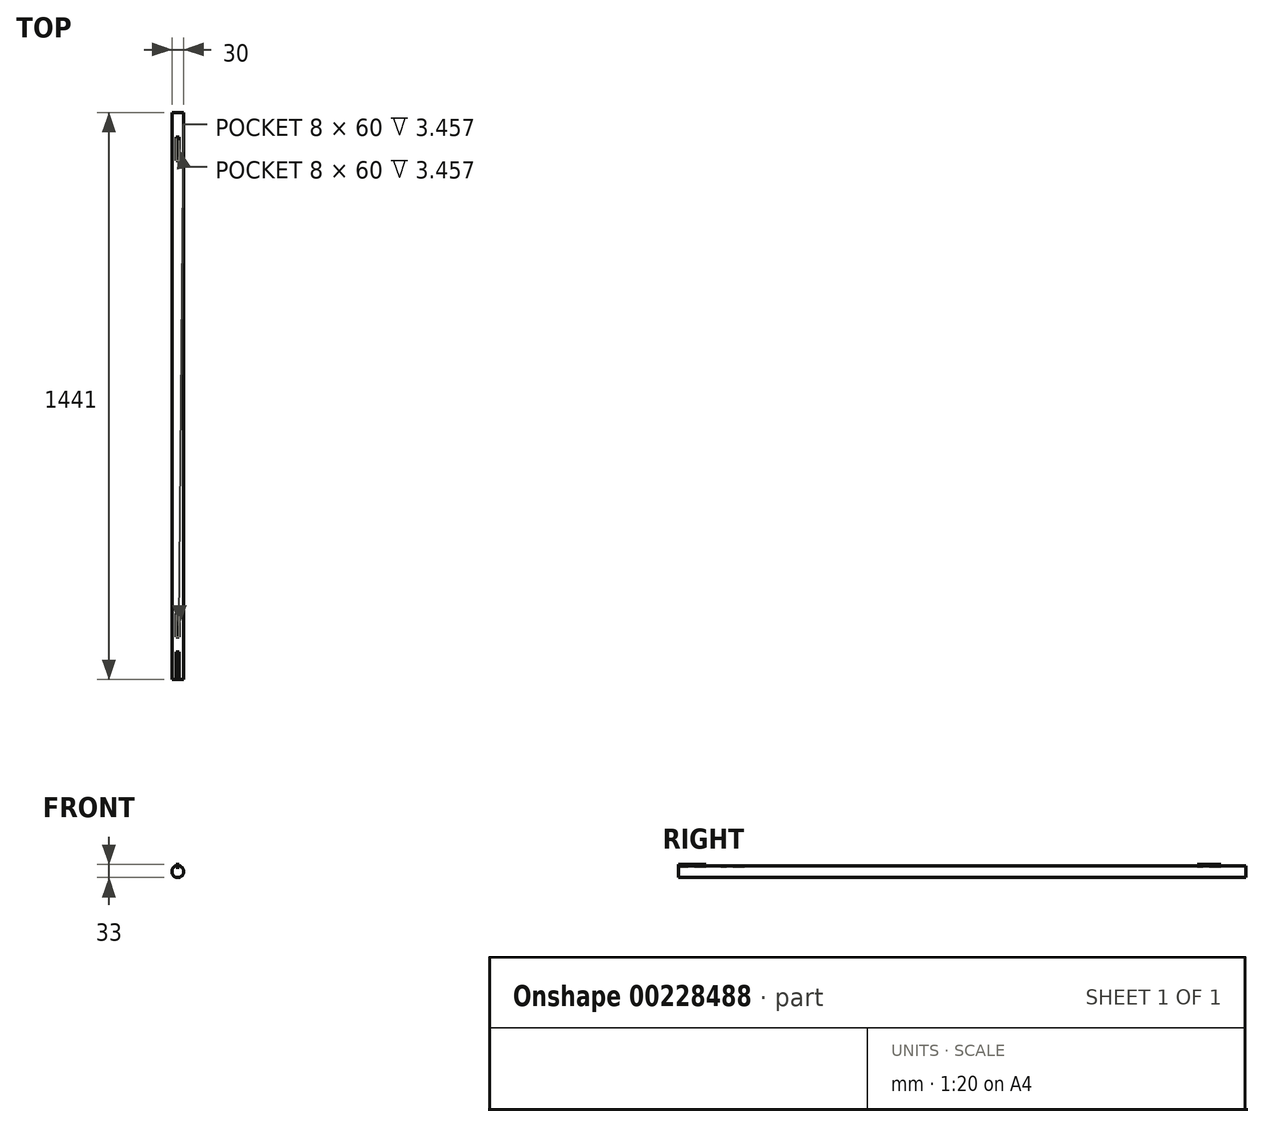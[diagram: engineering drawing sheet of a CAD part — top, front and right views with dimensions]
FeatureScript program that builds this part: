
annotation { "Feature Type Name" : "Feature", "Feature Type Description" : "" }
export const myFeature = defineFeature(function(context is Context, id is Id, definition is map)
    precondition{}
    {
        {
            var Q0;
            Q0=qCreatedBy(makeId("Front.planeOp"),FACE);
            var sketch = newSketch(context, id + "F0", { "sketchPlane" : qUnion([Q0])});
            skCircle(sketch, "E0", {"center": v(0, 0) * mm, "radius": 15 * mm});
            skSolve(sketch);
        }
        {
            var Q0;
            Q0=qSketchRegion(id+"F0",true);
            extrude(context, id + "F1", {"entities" : qUnion([Q0]), "depth" : (1441 - 698) * mm, "offsetDistance" : 25 * mm, "hasSecondDirection" : true, "secondDirectionOppositeDirection" : true, "secondDirectionDepth" : (1240 / 2 + 78) * mm});
        }
        {
            var Q0;
            Q0=qCreatedBy(makeId("Top.planeOp"),FACE);
            cPlane(context, id + "F2", {"entities" : qUnion([Q0]), "cplaneType" : CPlaneType.OFFSET, "offset" : 15 * mm, "width" : 150 * mm, "height" : 150 * mm});
        }
        {
            var Q0;
            Q0=qCreatedBy(id+"F2.planeOp",FACE);
            var sketch = newSketch(context, id + "F3", { "sketchPlane" : qUnion([Q0])});
            skLineSegment(sketch, "E1.bottom", {"start": v(-4, 635) * mm, "end": v(4, 635) * mm});
            skLineSegment(sketch, "E1.top", {"start": v(-4, 575) * mm, "end": v(4, 575) * mm});
            skLineSegment(sketch, "E1.left", {"start": v(-4, 635) * mm, "end": v(-4, 575) * mm});
            skLineSegment(sketch, "E1.right", {"start": v(4, 635) * mm, "end": v(4, 575) * mm});
            skLineSegment(sketch, "E2.bottom", {"start": v(-4, -575) * mm, "end": v(4, -575) * mm});
            skLineSegment(sketch, "E2.top", {"start": v(-4, -635) * mm, "end": v(4, -635) * mm});
            skLineSegment(sketch, "E2.left", {"start": v(-4, -575) * mm, "end": v(-4, -635) * mm});
            skLineSegment(sketch, "E2.right", {"start": v(4, -575) * mm, "end": v(4, -635) * mm});
            skLineSegment(sketch, "E3.bottom", {"start": v(-4, -673) * mm, "end": v(4, -673) * mm});
            skLineSegment(sketch, "E3.top", {"start": v(-4, -743) * mm, "end": v(4, -743) * mm});
            skLineSegment(sketch, "E3.left", {"start": v(-4, -673) * mm, "end": v(-4, -743) * mm});
            skLineSegment(sketch, "E3.right", {"start": v(4, -673) * mm, "end": v(4, -743) * mm});
            skSolve(sketch);
        }
        {
            var Q0;
            Q0 = qSketchRegion(id + "F3", true);
            extrude(context, id + "F4", {"entities" : qUnion([Q0]), "operationType" : NewBodyOperationType.REMOVE, "oppositeDirection" : true, "depth" : 4 * mm, "offsetDistance" : 25 * mm});
        }
        {
            var Q0;
            Q0=makeQuery(id+"F4.boolean.opBoolean","COPY",FACE,{"derivedFrom":makeQuery(id+"F4.opExtrude","CAP_FACE",FACE,{"disambiguationData":[OSD([sQuery(id+"F3.wireOp",EDGE,"E3.bottom"),sQuery(id+"F3.wireOp",EDGE,"E3.top"),sQuery(id+"F3.wireOp",EDGE,"E3.left"),sQuery(id+"F3.wireOp",EDGE,"E3.right")])],"isStart":false})});
            var Q1;
            Q1=makeQuery(id+"F4.boolean.opBoolean","COPY",FACE,{"derivedFrom":makeQuery(id+"F4.opExtrude","CAP_FACE",FACE,{"disambiguationData":[OSD([sQuery(id+"F3.wireOp",EDGE,"E1.bottom"),sQuery(id+"F3.wireOp",EDGE,"E1.top"),sQuery(id+"F3.wireOp",EDGE,"E1.left"),sQuery(id+"F3.wireOp",EDGE,"E1.right")])],"isStart":false})});
            extrude(context, id + "F5", {"entities" : qUnion([Q0, Q1]), "depth" : 7 * mm, "offsetDistance" : 25 * mm});
        }
    });
